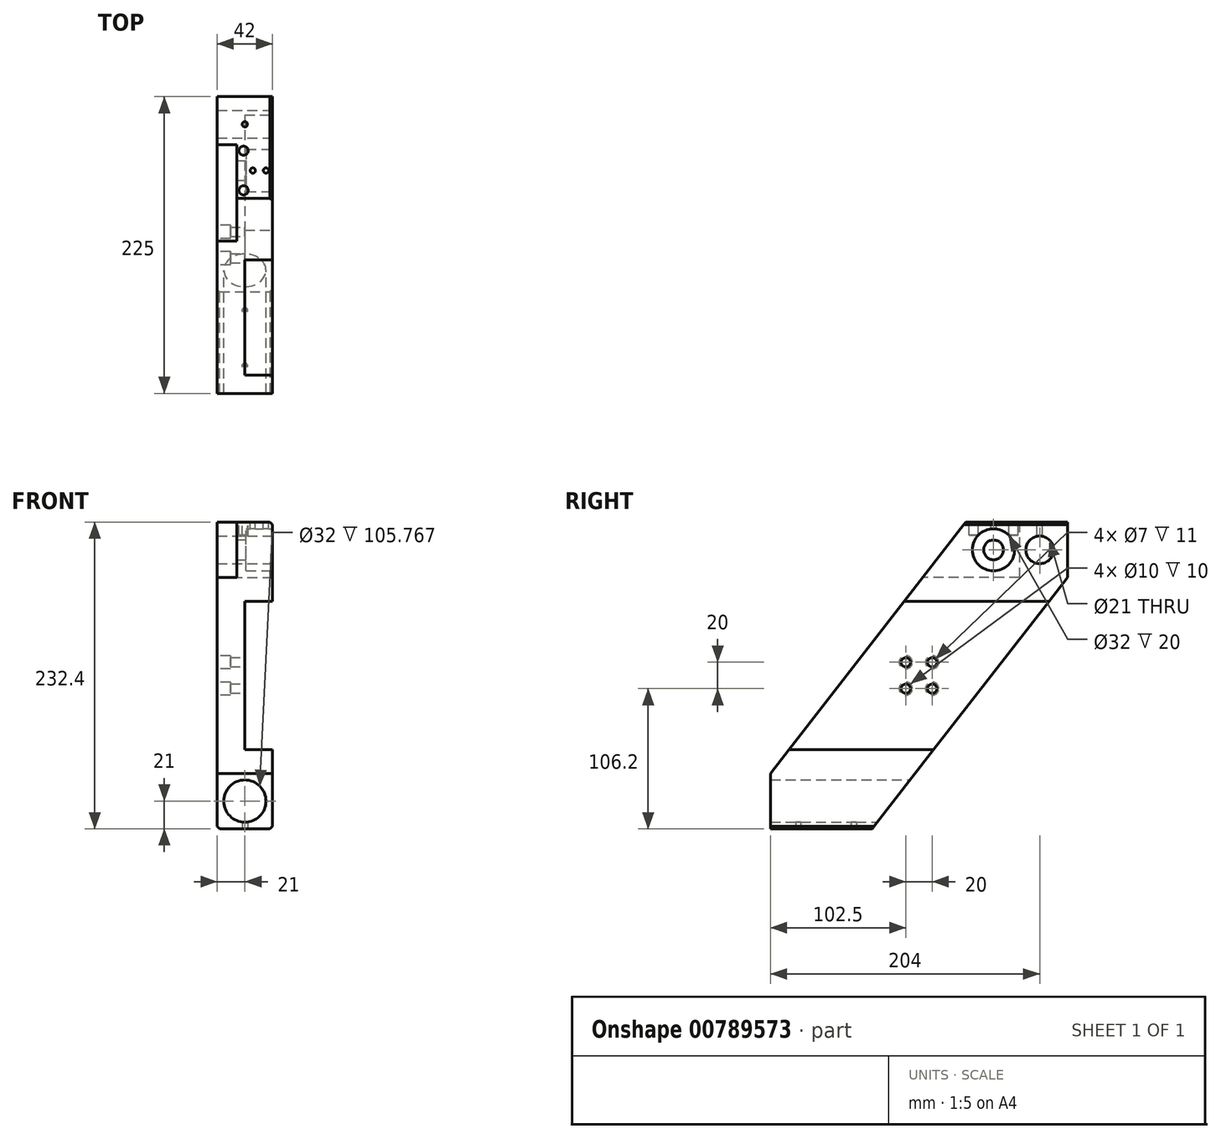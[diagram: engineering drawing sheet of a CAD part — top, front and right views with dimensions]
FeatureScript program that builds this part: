
annotation { "Feature Type Name" : "Feature", "Feature Type Description" : "" }
export const myFeature = defineFeature(function(context is Context, id is Id, definition is map)
    precondition{}
    {
        {
            var Q0;
            Q0=qCreatedBy(makeId("Right.planeOp"),FACE);
            var sketch = newSketch(context, id + "F0", { "sketchPlane" : qUnion([Q0])});
            skLineSegment(sketch, "E0.bottom", {"start": v(112.5, 116.2) * mm, "end": v(35.5, 116.2) * mm});
            skLineSegment(sketch, "E0.top", {"start": v(112.5, -116.2) * mm, "end": v(70.5, -116.2) * mm});
            skLineSegment(sketch, "E0.left", {"start": v(112.5, 116.2) * mm, "end": v(112.5, 74.2) * mm});
            skLineSegment(sketch, "E0.right", {"start": v(-112.5, 116.2) * mm, "end": v(-112.5, 74.2) * mm});
            skCircle(sketch, "E1", {"center": v(56.5, 95.2) * mm, "radius": 7.5 * mm});
            skCircle(sketch, "E2", {"center": v(-91.5, 95.2) * mm, "radius": 10.5 * mm});
            skPoint(sketch, "E3", {"position": v(0, 0) * mm});
            skPoint(sketch, "E4.start.orphan", {"position": v(112.5, 116.2) * mm});
            skPoint(sketch, "E5.trimOffspring.end.orphan", {"position": v(-112.5, 116.2) * mm});
            skCircle(sketch, "E6", {"center": v(91.5, 95.2) * mm, "radius": 10.5 * mm});
            skPoint(sketch, "E7", {"position": v(-35.5, -116.2) * mm});
            skPoint(sketch, "E8", {"position": v(70.5, -116.2) * mm});
            skPoint(sketch, "E9", {"position": v(112.5, -74.2) * mm});
            skPoint(sketch, "E10", {"position": v(-112.5, -74.2) * mm});
            skPoint(sketch, "E11", {"position": v(112.5, 74.2) * mm});
            skPoint(sketch, "E12", {"position": v(-112.5, 74.2) * mm});
            skLineSegment(sketch, "E13", {"start": v(112.5, 74.2) * mm, "end": v(-35.5, -116.2) * mm});
            skLineSegment(sketch, "E14", {"start": v(70.5, -116.2) * mm, "end": v(-112.5, 74.2) * mm});
            skPoint(sketch, "E15", {"position": v(35.5, 116.2) * mm});
            skPoint(sketch, "E16", {"position": v(-70.5, 116.2) * mm});
            skLineSegment(sketch, "E17", {"start": v(35.5, 116.2) * mm, "end": v(-112.5, -74.2) * mm});
            skLineSegment(sketch, "E18", {"start": v(112.5, -74.2) * mm, "end": v(-70.5, 116.2) * mm});
            skLineSegment(sketch, "E19.trimOffspring", {"start": v(-70.5, 116.2) * mm, "end": v(-112.5, 116.2) * mm});
            skLineSegment(sketch, "E20.trimOffspring", {"start": v(-112.5, -74.2) * mm, "end": v(-112.5, -116.2) * mm});
            skLineSegment(sketch, "E21.trimOffspring", {"start": v(-35.5, -116.2) * mm, "end": v(-112.5, -116.2) * mm});
            skLineSegment(sketch, "E22.trimOffspring", {"start": v(112.5, -74.2) * mm, "end": v(112.5, -116.2) * mm});
            skPoint(sketch, "E23", {"position": v(10, 10) * mm});
            skPoint(sketch, "E24", {"position": v(10, -10) * mm});
            skPoint(sketch, "E25", {"position": v(-10, -10) * mm});
            skPoint(sketch, "E26", {"position": v(-10, 10) * mm});
            skCircle(sketch, "E27", {"center": v(10, 10) * mm, "radius": 3.5 * mm});
            skCircle(sketch, "E28", {"center": v(-10, 10) * mm, "radius": 3.5 * mm});
            skCircle(sketch, "E29", {"center": v(10, -10) * mm, "radius": 3.5 * mm});
            skCircle(sketch, "E30", {"center": v(-10, -10) * mm, "radius": 3.5 * mm});
            skSolve(sketch);
        }
        {
            var Q0;
            {var subQ6=sQuery(id+"F0.wireOp",EDGE,"E0.bottom");Q0=makeQuery(id+"F0.imprint","IMPRINT",FACE,{"disambiguationData":[TD([[makeQuery(id+"F0.imprint","IMPRINT",EDGE,{"derivedFrom":subQ6}),1.0]])]});}
            var Q1;
            Q1=makeQuery(id+"F0.imprint","IMPRINT",FACE,{"disambiguationData":[TD([[makeQuery(id+"F0.imprint","IMPRINT",EDGE,{"derivedFrom":sQuery(id+"F0.wireOp",EDGE,"E27")}),-1.0]])]});
            var Q2;
            {var subQ0=sQuery(id+"F0.wireOp",EDGE,"E20.trimOffspring");Q2=makeQuery(id+"F0.imprint","IMPRINT",FACE,{"disambiguationData":[TD([[makeQuery(id+"F0.imprint","IMPRINT",EDGE,{"derivedFrom":subQ0}),1.0]])]});}
            extrude(context, id + "F1", {"entities" : qUnion([Q0, Q1, Q2]), "oppositeDirection" : true, "depth" : 42 * mm, "offsetDistance" : 25 * mm});
        }
        {
            var Q0;
            Q0=makeQuery(id+"F1.opExtrude","CAP_FACE",FACE,{"disambiguationData":[OSD([sQuery(id+"F0.wireOp",EDGE,"E0.bottom"),sQuery(id+"F0.wireOp",EDGE,"E0.left"),sQuery(id+"F0.wireOp",EDGE,"E1"),sQuery(id+"F0.wireOp",EDGE,"E6"),sQuery(id+"F0.wireOp",EDGE,"E13"),sQuery(id+"F0.wireOp",EDGE,"E17"),sQuery(id+"F0.wireOp",EDGE,"E20.trimOffspring"),sQuery(id+"F0.wireOp",EDGE,"E21.trimOffspring"),sQuery(id+"F0.wireOp",EDGE,"E27"),sQuery(id+"F0.wireOp",EDGE,"E28"),sQuery(id+"F0.wireOp",EDGE,"E29"),sQuery(id+"F0.wireOp",EDGE,"E30")])],"isStart":false});
            var sketch = newSketch(context, id + "F2", { "sketchPlane" : qUnion([Q0])});
            skCircle(sketch, "E31", {"center": v(-10, 10) * mm, "radius": 5 * mm});
            skCircle(sketch, "E32", {"center": v(10, 10) * mm, "radius": 5 * mm});
            skCircle(sketch, "E33", {"center": v(10, -10) * mm, "radius": 5 * mm});
            skCircle(sketch, "E34", {"center": v(-10, -10) * mm, "radius": 5 * mm});
            skSolve(sketch);
        }
        {
            var Q0;
            Q0=makeQuery(id+"F2.imprint","IMPRINT",FACE,{"disambiguationData":[TD([[makeQuery(id+"F2.imprint","IMPRINT",EDGE,{"derivedFrom":sQuery(id+"F2.wireOp",EDGE,"E31")}),1.0]])]});
            var Q1;
            Q1=makeQuery(id+"F2.imprint","IMPRINT",FACE,{"disambiguationData":[TD([[makeQuery(id+"F2.imprint","IMPRINT",EDGE,{"derivedFrom":sQuery(id+"F2.wireOp",EDGE,"E34")}),1.0]])]});
            var Q2;
            Q2=makeQuery(id+"F2.imprint","IMPRINT",FACE,{"disambiguationData":[TD([[makeQuery(id+"F2.imprint","IMPRINT",EDGE,{"derivedFrom":sQuery(id+"F2.wireOp",EDGE,"E32")}),1.0]])]});
            var Q3;
            Q3=makeQuery(id+"F2.imprint","IMPRINT",FACE,{"disambiguationData":[TD([[makeQuery(id+"F2.imprint","IMPRINT",EDGE,{"derivedFrom":sQuery(id+"F2.wireOp",EDGE,"E33")}),1.0]])]});
            extrude(context, id + "F3", {"entities" : qUnion([Q0, Q1, Q2, Q3]), "operationType" : NewBodyOperationType.REMOVE, "oppositeDirection" : true, "depth" : 10 * mm, "offsetDistance" : 25 * mm});
        }
        {
            var Q0;
            Q0=makeQuery(id+"F1.opExtrude","CAP_FACE",FACE,{"disambiguationData":[OSD([sQuery(id+"F0.wireOp",EDGE,"E0.bottom"),sQuery(id+"F0.wireOp",EDGE,"E0.left"),sQuery(id+"F0.wireOp",EDGE,"E1"),sQuery(id+"F0.wireOp",EDGE,"E6"),sQuery(id+"F0.wireOp",EDGE,"E13"),sQuery(id+"F0.wireOp",EDGE,"E17"),sQuery(id+"F0.wireOp",EDGE,"E20.trimOffspring"),sQuery(id+"F0.wireOp",EDGE,"E21.trimOffspring"),sQuery(id+"F0.wireOp",EDGE,"E27"),sQuery(id+"F0.wireOp",EDGE,"E28"),sQuery(id+"F0.wireOp",EDGE,"E29"),sQuery(id+"F0.wireOp",EDGE,"E30")])],"isStart":true});
            var sketch = newSketch(context, id + "F4", { "sketchPlane" : qUnion([Q0])});
            skLineSegment(sketch, "E35", {"start": v(98.5, 56.2) * mm, "end": v(11.14, -56.2) * mm});
            skLineSegment(sketch, "E36", {"start": v(11.14, -56.2) * mm, "end": v(-98.5, -56.2) * mm});
            skLineSegment(sketch, "E37", {"start": v(-11.14, 56.2) * mm, "end": v(-98.5, -56.2) * mm});
            skLineSegment(sketch, "E38", {"start": v(98.5, 56.2) * mm, "end": v(-11.14, 56.2) * mm});
            skLineSegment(sketch, "E39", {"start": v(-98.5, -56.2) * mm, "end": v(-11.14, 56.2) * mm});
            skSolve(sketch);
        }
        {
            var Q0;
            Q0=makeQuery(id+"F4.imprint","IMPRINT",FACE,{"disambiguationData":[TD([[makeQuery(id+"F4.imprint","IMPRINT",EDGE,{"derivedFrom":sQuery(id+"F4.wireOp",EDGE,"E36")}),-1.0]])]});
            extrude(context, id + "F5", {"entities" : qUnion([Q0]), "operationType" : NewBodyOperationType.REMOVE, "oppositeDirection" : true, "depth" : 21 * mm, "offsetDistance" : 25 * mm});
        }
        {
            var Q0;
            Q0=makeQuery(id+"F1.opExtrude","SWEPT_FACE",FACE,{"disambiguationData":[OSD([sQuery(id+"F0.wireOp",EDGE,"E0.left")])]});
            var sketch = newSketch(context, id + "F6", { "sketchPlane" : qUnion([Q0])});
            skPoint(sketch, "E40", {"position": v(21, -95.2) * mm});
            skCircle(sketch, "E41", {"center": v(21, -95.2) * mm, "radius": 16 * mm});
            skSolve(sketch);
        }
        {
            var Q0;
            Q0=makeQuery(id+"F6.imprint","IMPRINT",FACE,{"disambiguationData":[TD([[makeQuery(id+"F6.imprint","IMPRINT",EDGE,{"derivedFrom":sQuery(id+"F6.wireOp",EDGE,"E41")}),1.0]])]});
            extrude(context, id + "F7", {"entities" : qUnion([Q0]), "operationType" : NewBodyOperationType.REMOVE, "oppositeDirection" : true, "depth" : 250 * mm, "offsetDistance" : 25 * mm});
        }
        {
            var Q0;
            Q0=makeQuery(id+"F1.opExtrude","SWEPT_FACE",FACE,{"disambiguationData":[OSD([sQuery(id+"F0.wireOp",EDGE,"E21.trimOffspring")])]});
            var sketch = newSketch(context, id + "F8", { "sketchPlane" : qUnion([Q0])});
            skPoint(sketch, "E42", {"position": v(-21, 91.5) * mm});
            skPoint(sketch, "E42.positionSnap0", {"position": v(-21, 112.5) * mm});
            skPoint(sketch, "E43", {"position": v(-21, 49.5) * mm});
            skCircle(sketch, "E44", {"center": v(-21, 91.5) * mm, "radius": 2 * mm});
            skCircle(sketch, "E45", {"center": v(-21, 49.5) * mm, "radius": 2 * mm});
            skSolve(sketch);
        }
        {
            var Q0;
            Q0=makeQuery(id+"F8.imprint","IMPRINT",FACE,{"disambiguationData":[TD([[makeQuery(id+"F8.imprint","IMPRINT",EDGE,{"derivedFrom":sQuery(id+"F8.wireOp",EDGE,"E45")}),1.0]])]});
            var Q1;
            Q1=makeQuery(id+"F8.imprint","IMPRINT",FACE,{"disambiguationData":[TD([[makeQuery(id+"F8.imprint","IMPRINT",EDGE,{"derivedFrom":sQuery(id+"F8.wireOp",EDGE,"E44")}),1.0]])]});
            extrude(context, id + "F9", {"entities" : qUnion([Q0, Q1]), "operationType" : NewBodyOperationType.REMOVE, "oppositeDirection" : true, "depth" : 25 * mm, "offsetDistance" : 25 * mm});
        }
        {
            var Q0;
            Q0=makeQuery(id+"F1.opExtrude","CAP_FACE",FACE,{"disambiguationData":[OSD([sQuery(id+"F0.wireOp",EDGE,"E0.bottom"),sQuery(id+"F0.wireOp",EDGE,"E0.left"),sQuery(id+"F0.wireOp",EDGE,"E1"),sQuery(id+"F0.wireOp",EDGE,"E6"),sQuery(id+"F0.wireOp",EDGE,"E13"),sQuery(id+"F0.wireOp",EDGE,"E17"),sQuery(id+"F0.wireOp",EDGE,"E20.trimOffspring"),sQuery(id+"F0.wireOp",EDGE,"E21.trimOffspring"),sQuery(id+"F0.wireOp",EDGE,"E27"),sQuery(id+"F0.wireOp",EDGE,"E28"),sQuery(id+"F0.wireOp",EDGE,"E29"),sQuery(id+"F0.wireOp",EDGE,"E30")])],"isStart":false});
            var sketch = newSketch(context, id + "F10", { "sketchPlane" : qUnion([Q0])});
            skLineSegment(sketch, "E46", {"start": v(-76, 116.39) * mm, "end": v(-76, 74.39) * mm});
            skLineSegment(sketch, "E47", {"start": v(-76, 74.39) * mm, "end": v(-3, 74.39) * mm});
            skLineSegment(sketch, "E48", {"start": v(-3, 74.39) * mm, "end": v(-3, 116.39) * mm});
            skLineSegment(sketch, "E49", {"start": v(-3, 116.39) * mm, "end": v(-76, 116.39) * mm});
            skSolve(sketch);
        }
        {
            var Q0;
            {var subQ8=sQuery(id+"F10.wireOp",EDGE,"E47");Q0=makeQuery(id+"F10.imprint","IMPRINT",FACE,{"disambiguationData":[TD([[makeQuery(id+"F10.imprint","IMPRINT",EDGE,{"derivedFrom":subQ8}),1.0]])]});}
            var Q1;
            {var subQ8=sQuery(id+"F10.wireOp",EDGE,"E48");Q1=makeQuery(id+"F10.imprint","IMPRINT",FACE,{"disambiguationData":[TD([[makeQuery(id+"F10.imprint","IMPRINT",EDGE,{"derivedFrom":subQ8}),1.0]])]});}
            extrude(context, id + "F11", {"entities" : qUnion([Q0, Q1]), "operationType" : NewBodyOperationType.REMOVE, "oppositeDirection" : true, "depth" : 15 * mm, "offsetDistance" : 25 * mm});
        }
        {
            var Q0;
            Q0=makeQuery(id+"F1.opExtrude","SWEPT_FACE",FACE,{"disambiguationData":[OSD([sQuery(id+"F0.wireOp",EDGE,"E0.bottom")])]});
            var sketch = newSketch(context, id + "F12", { "sketchPlane" : qUnion([Q0])});
            skPoint(sketch, "E50", {"position": v(-21, 91.5) * mm});
            skPoint(sketch, "E50.positionSnap0", {"position": v(-21, 112.5) * mm});
            skCircle(sketch, "E51", {"center": v(-21, 91.5) * mm, "radius": 2 * mm});
            skPoint(sketch, "E52", {"position": v(-5, 56.5) * mm});
            skPoint(sketch, "E53", {"position": v(-15, 56.5) * mm});
            skCircle(sketch, "E54", {"center": v(-5, 56.5) * mm, "radius": 2 * mm});
            skCircle(sketch, "E55", {"center": v(-15, 56.5) * mm, "radius": 2 * mm});
            skPoint(sketch, "E56", {"position": v(-22, 71.5) * mm});
            skPoint(sketch, "E57", {"position": v(-22, 41.5) * mm});
            skCircle(sketch, "E58", {"center": v(-22, 71.5) * mm, "radius": 3.5 * mm});
            skCircle(sketch, "E59", {"center": v(-22, 41.5) * mm, "radius": 3.5 * mm});
            skSolve(sketch);
        }
        {
            var Q0;
            Q0=makeQuery(id+"F12.imprint","IMPRINT",FACE,{"disambiguationData":[TD([[makeQuery(id+"F12.imprint","IMPRINT",EDGE,{"derivedFrom":sQuery(id+"F12.wireOp",EDGE,"E51")}),1.0]])]});
            var Q1;
            Q1=makeQuery(id+"F12.imprint","IMPRINT",FACE,{"disambiguationData":[TD([[makeQuery(id+"F12.imprint","IMPRINT",EDGE,{"derivedFrom":sQuery(id+"F12.wireOp",EDGE,"E55")}),1.0]])]});
            var Q2;
            Q2=makeQuery(id+"F12.imprint","IMPRINT",FACE,{"disambiguationData":[TD([[makeQuery(id+"F12.imprint","IMPRINT",EDGE,{"derivedFrom":sQuery(id+"F12.wireOp",EDGE,"E54")}),1.0]])]});
            extrude(context, id + "F13", {"entities" : qUnion([Q0, Q1, Q2]), "operationType" : NewBodyOperationType.REMOVE, "oppositeDirection" : true, "depth" : 25 * mm, "offsetDistance" : 25 * mm});
        }
        {
            var Q0;
            {var subQ3=sQuery(id+"F4.wireOp",EDGE,"E38");Q0=makeQuery(id+"F4.imprint","IMPRINT",FACE,{"disambiguationData":[TD([[makeQuery(id+"F4.imprint","IMPRINT",EDGE,{"derivedFrom":subQ3}),-1.0]])]});}
            var sketch = newSketch(context, id + "F14", { "sketchPlane" : qUnion([Q0])});
            skPoint(sketch, "E60", {"position": v(56.5, 95.2) * mm});
            skCircle(sketch, "E61", {"center": v(56.5, 95.2) * mm, "radius": 16 * mm});
            skSolve(sketch);
        }
        {
            var Q0;
            Q0=qSketchRegion(id+"F14",true);
            extrude(context, id + "F15", {"entities" : qUnion([Q0]), "operationType" : NewBodyOperationType.REMOVE, "oppositeDirection" : true, "depth" : 20 * mm, "offsetDistance" : 25 * mm});
        }
        {
            var Q0;
            Q0=makeQuery(id+"F5.boolean.opBoolean","COPY",EDGE,{"derivedFrom":makeQuery(id+"F5.opExtrude","CAP_EDGE",EDGE,{"disambiguationData":[OSD([sQuery(id+"F4.wireOp",EDGE,"E38")])],"isStart":true})});
            var Q1;
            Q1=makeQuery(id+"F5.boolean.opBoolean","COPY",EDGE,{"derivedFrom":makeQuery(id+"F5.opExtrude","CAP_EDGE",EDGE,{"disambiguationData":[OSD([sQuery(id+"F4.wireOp",EDGE,"E36")])],"isStart":true})});
            var Q2;
            Q2=makeQuery(id+"F1.opExtrude","CAP_EDGE",EDGE,{"disambiguationData":[OSD([sQuery(id+"F0.wireOp",EDGE,"E21.trimOffspring")])],"isStart":false});
            var Q3;
            Q3=makeQuery(id+"F1.opExtrude","CAP_EDGE",EDGE,{"disambiguationData":[OSD([sQuery(id+"F0.wireOp",EDGE,"E21.trimOffspring")])],"isStart":true});
            var Q4;
            Q4=makeQuery(id+"F1.opExtrude","CAP_EDGE",EDGE,{"disambiguationData":[OSD([sQuery(id+"F0.wireOp",EDGE,"E0.bottom")])],"isStart":true});
            var Q5;
            Q5=makeQuery(id+"F5.boolean.opBoolean","COPY",EDGE,{"derivedFrom":makeQuery(id+"F5.opExtrude","CAP_EDGE",EDGE,{"disambiguationData":[OSD([sQuery(id+"F4.wireOp",EDGE,"E39")])],"isStart":false})});
            var Q6;
            Q6=makeQuery(id+"F5.boolean.opBoolean","COPY",EDGE,{"derivedFrom":makeQuery(id+"F5.opExtrude","CAP_EDGE",EDGE,{"disambiguationData":[OSD([sQuery(id+"F4.wireOp",EDGE,"E35")])],"isStart":false})});
            var Q7;
            Q7=makeQuery(id+"F11.boolean.opBoolean","COPY",EDGE,{"derivedFrom":makeQuery(id+"F11.opExtrude","CAP_EDGE",EDGE,{"disambiguationData":[OSD([sQuery(id+"F10.wireOp",EDGE,"E47")])],"isStart":true})});
            var Q8;
            Q8=makeQuery(id+"F11.boolean.opBoolean","COPY",EDGE,{"derivedFrom":makeQuery(id+"F11.opExtrude","CAP_EDGE",EDGE,{"disambiguationData":[OSD([sQuery(id+"F10.wireOp",EDGE,"E46")])],"isStart":true})});
            chamfer(context, id + "F16", {"entities" : qUnion([Q0, Q1, Q2, Q3, Q4, Q5, Q6, Q7, Q8]), "width" : 2 * mm, "tangentPropagation" : true});
        }
        {
            var Q0;
            Q0=makeQuery(id+"F12.imprint","IMPRINT",FACE,{"disambiguationData":[TD([[makeQuery(id+"F12.imprint","IMPRINT",EDGE,{"derivedFrom":sQuery(id+"F12.wireOp",EDGE,"E58")}),1.0]])]});
            var Q1;
            Q1=makeQuery(id+"F12.imprint","IMPRINT",FACE,{"disambiguationData":[TD([[makeQuery(id+"F12.imprint","IMPRINT",EDGE,{"derivedFrom":sQuery(id+"F12.wireOp",EDGE,"E59")}),1.0]])]});
            extrude(context, id + "F17", {"entities" : qUnion([Q0, Q1]), "operationType" : NewBodyOperationType.REMOVE, "oppositeDirection" : true, "depth" : 10 * mm, "offsetDistance" : 25 * mm});
        }
    });
